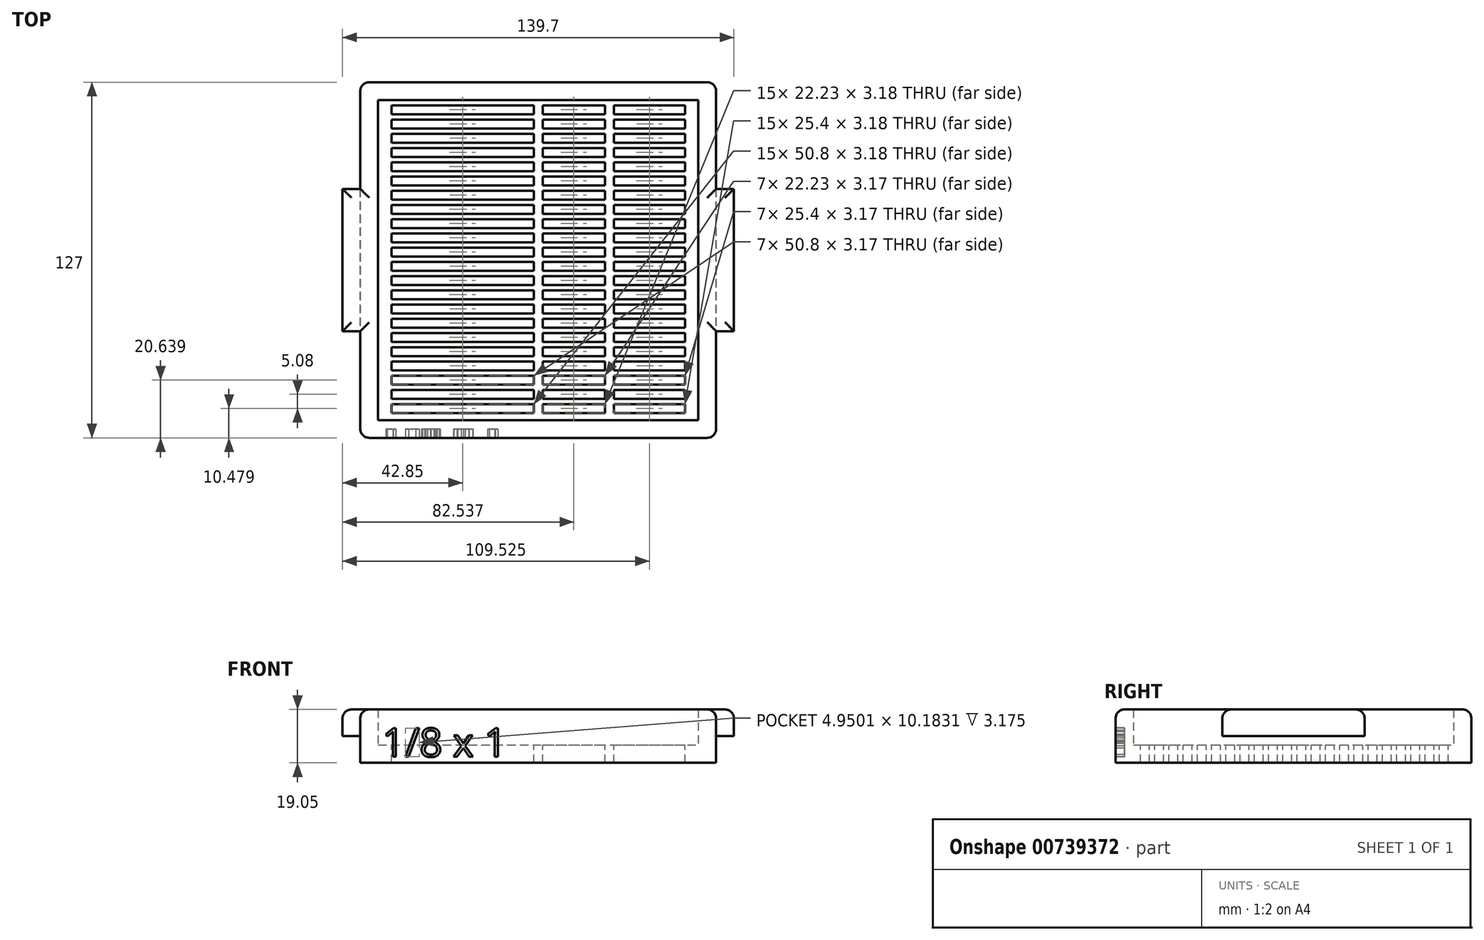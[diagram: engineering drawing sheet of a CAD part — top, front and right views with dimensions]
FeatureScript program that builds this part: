
annotation { "Feature Type Name" : "Feature", "Feature Type Description" : "" }
export const myFeature = defineFeature(function(context is Context, id is Id, definition is map)
    precondition{}
    {
        {
            var Q0;
            Q0=qCreatedBy(makeId("Top.planeOp"),FACE);
            var sketch = newSketch(context, id + "F0", { "sketchPlane" : qUnion([Q0])});
            skLineSegment(sketch, "E0.bottom", {"start": v(-63.5, -63.76) * mm, "end": v(63.5, -63.76) * mm});
            skLineSegment(sketch, "E0.top", {"start": v(-63.5, 63.24) * mm, "end": v(63.5, 63.24) * mm});
            skLineSegment(sketch, "E0.left", {"start": v(-63.5, -63.76) * mm, "end": v(-63.5, 63.24) * mm});
            skLineSegment(sketch, "E0.right", {"start": v(63.5, -63.76) * mm, "end": v(63.5, 63.24) * mm});
            skLineSegment(sketch, "E1.bottom", {"start": v(-57.15, -57.4) * mm, "end": v(57.15, -57.4) * mm});
            skLineSegment(sketch, "E1.top", {"start": v(-57.15, 56.9) * mm, "end": v(57.15, 56.9) * mm});
            skLineSegment(sketch, "E1.left", {"start": v(-57.15, -57.4) * mm, "end": v(-57.15, 56.9) * mm});
            skLineSegment(sketch, "E1.right", {"start": v(57.15, -57.4) * mm, "end": v(57.15, 56.9) * mm});
            skPoint(sketch, "E2", {"position": v(-63.5, -0.26) * mm});
            skPoint(sketch, "E3", {"position": v(63.5, -0.26) * mm});
            skLineSegment(sketch, "E4.bottom", {"start": v(-69.85, 25.14) * mm, "end": v(-57.15, 25.14) * mm});
            skLineSegment(sketch, "E4.top", {"start": v(-69.85, -25.66) * mm, "end": v(-57.15, -25.66) * mm});
            skLineSegment(sketch, "E4.left", {"start": v(-69.85, 25.14) * mm, "end": v(-69.85, -25.66) * mm});
            skLineSegment(sketch, "E4.right", {"start": v(-57.15, 25.14) * mm, "end": v(-57.15, -25.66) * mm});
            skLineSegment(sketch, "E5.bottom", {"start": v(69.85, 25.14) * mm, "end": v(57.15, 25.14) * mm});
            skLineSegment(sketch, "E5.top", {"start": v(69.85, -25.66) * mm, "end": v(57.15, -25.66) * mm});
            skLineSegment(sketch, "E5.left", {"start": v(69.85, 25.14) * mm, "end": v(69.85, -25.66) * mm});
            skLineSegment(sketch, "E5.right", {"start": v(57.15, 25.14) * mm, "end": v(57.15, -25.66) * mm});
            skPoint(sketch, "E5.cornerSnap0", {"position": v(-63.5, 25.14) * mm});
            skSolve(sketch);
        }
        {
            var Q0;
            {var subQ3=sQuery(id+"F0.wireOp",EDGE,"E1.bottom");Q0=makeQuery(id+"F0.imprint","IMPRINT",FACE,{"disambiguationData":[TD([[makeQuery(id+"F0.imprint","IMPRINT",EDGE,{"derivedFrom":subQ3}),1.0]])]});}
            extrude(context, id + "F1", {"entities" : qUnion([Q0]), "depth" : 6.35 * mm, "offsetDistance" : 25.4 * mm});
        }
        {
            var Q0;
            Q0 = qSketchRegion(id + "F0", true);
            extrude(context, id + "F2", {"entities" : qUnion([Q0]), "operationType" : NewBodyOperationType.ADD, "depth" : 19.05 * mm, "offsetDistance" : 25.4 * mm});
        }
        {
            var Q0;
            Q0=makeQuery(id+"F1.opExtrude","CAP_FACE",FACE,{"disambiguationData":[OSD([sQuery(id+"F0.wireOp",EDGE,"E1.bottom"),sQuery(id+"F0.wireOp",EDGE,"E1.top"),sQuery(id+"F0.wireOp",EDGE,"E1.left"),sQuery(id+"F0.wireOp",EDGE,"E1.right"),sQuery(id+"F0.wireOp",EDGE,"E4.right"),sQuery(id+"F0.wireOp",EDGE,"E5.right")])],"isStart":false});
            var sketch = newSketch(context, id + "F3", { "sketchPlane" : qUnion([Q0])});
            skLineSegment(sketch, "E6.bottom", {"start": v(-52.4, -54.87) * mm, "end": v(-23.83, -54.87) * mm});
            skLineSegment(sketch, "E6.top", {"start": v(-52.4, -51.7) * mm, "end": v(-23.83, -51.7) * mm});
            skLineSegment(sketch, "E6.left", {"start": v(-52.4, -54.87) * mm, "end": v(-52.4, -51.7) * mm});
            skLineSegment(sketch, "E6.right", {"start": v(-23.83, -54.87) * mm, "end": v(-23.83, -51.7) * mm});
            skLineSegment(sketch, "E7.0.1.0", {"start": v(-52.4, -49.79) * mm, "end": v(-23.83, -49.79) * mm});
            skLineSegment(sketch, "E7.0.1.1", {"start": v(-52.4, -46.61) * mm, "end": v(-23.83, -46.61) * mm});
            skLineSegment(sketch, "E7.0.1.2", {"start": v(-52.4, -49.79) * mm, "end": v(-52.4, -46.61) * mm});
            skLineSegment(sketch, "E7.0.1.3", {"start": v(-23.83, -49.79) * mm, "end": v(-23.83, -46.61) * mm});
            skLineSegment(sketch, "E7.0.2.0", {"start": v(-52.4, -44.7) * mm, "end": v(-23.83, -44.7) * mm});
            skLineSegment(sketch, "E7.0.2.1", {"start": v(-52.4, -41.53) * mm, "end": v(-23.83, -41.53) * mm});
            skLineSegment(sketch, "E7.0.2.2", {"start": v(-52.4, -44.7) * mm, "end": v(-52.4, -41.53) * mm});
            skLineSegment(sketch, "E7.0.2.3", {"start": v(-23.83, -44.7) * mm, "end": v(-23.83, -41.53) * mm});
            skLineSegment(sketch, "E7.0.3.0", {"start": v(-52.4, -39.63) * mm, "end": v(-23.83, -39.63) * mm});
            skLineSegment(sketch, "E7.0.3.1", {"start": v(-52.4, -36.45) * mm, "end": v(-23.83, -36.45) * mm});
            skLineSegment(sketch, "E7.0.3.2", {"start": v(-52.4, -39.63) * mm, "end": v(-52.4, -36.45) * mm});
            skLineSegment(sketch, "E7.0.3.3", {"start": v(-23.83, -39.63) * mm, "end": v(-23.83, -36.45) * mm});
            skLineSegment(sketch, "E7.0.4.0", {"start": v(-52.4, -34.55) * mm, "end": v(-23.83, -34.55) * mm});
            skLineSegment(sketch, "E7.0.4.1", {"start": v(-52.4, -31.37) * mm, "end": v(-23.83, -31.37) * mm});
            skLineSegment(sketch, "E7.0.4.2", {"start": v(-52.4, -34.55) * mm, "end": v(-52.4, -31.37) * mm});
            skLineSegment(sketch, "E7.0.4.3", {"start": v(-23.83, -34.55) * mm, "end": v(-23.83, -31.37) * mm});
            skLineSegment(sketch, "E7.0.5.0", {"start": v(-52.4, -29.47) * mm, "end": v(-23.83, -29.47) * mm});
            skLineSegment(sketch, "E7.0.5.1", {"start": v(-52.4, -26.3) * mm, "end": v(-23.83, -26.3) * mm});
            skLineSegment(sketch, "E7.0.5.2", {"start": v(-52.4, -29.47) * mm, "end": v(-52.4, -26.3) * mm});
            skLineSegment(sketch, "E7.0.5.3", {"start": v(-23.83, -29.47) * mm, "end": v(-23.83, -26.3) * mm});
            skLineSegment(sketch, "E7.0.6.0", {"start": v(-52.4, -24.39) * mm, "end": v(-23.83, -24.39) * mm});
            skLineSegment(sketch, "E7.0.6.1", {"start": v(-52.4, -21.21) * mm, "end": v(-23.83, -21.21) * mm});
            skLineSegment(sketch, "E7.0.6.2", {"start": v(-52.4, -24.39) * mm, "end": v(-52.4, -21.21) * mm});
            skLineSegment(sketch, "E7.0.6.3", {"start": v(-23.83, -24.39) * mm, "end": v(-23.83, -21.21) * mm});
            skLineSegment(sketch, "E7.0.7.0", {"start": v(-52.4, -19.3) * mm, "end": v(-23.83, -19.3) * mm});
            skLineSegment(sketch, "E7.0.7.1", {"start": v(-52.4, -16.13) * mm, "end": v(-23.83, -16.13) * mm});
            skLineSegment(sketch, "E7.0.7.2", {"start": v(-52.4, -19.3) * mm, "end": v(-52.4, -16.13) * mm});
            skLineSegment(sketch, "E7.0.7.3", {"start": v(-23.83, -19.3) * mm, "end": v(-23.83, -16.13) * mm});
            skLineSegment(sketch, "E7.0.8.0", {"start": v(-52.4, -14.23) * mm, "end": v(-23.83, -14.23) * mm});
            skLineSegment(sketch, "E7.0.8.1", {"start": v(-52.4, -11.05) * mm, "end": v(-23.83, -11.05) * mm});
            skLineSegment(sketch, "E7.0.8.2", {"start": v(-52.4, -14.23) * mm, "end": v(-52.4, -11.05) * mm});
            skLineSegment(sketch, "E7.0.8.3", {"start": v(-23.83, -14.23) * mm, "end": v(-23.83, -11.05) * mm});
            skLineSegment(sketch, "E7.0.9.0", {"start": v(-52.4, -9.15) * mm, "end": v(-23.83, -9.15) * mm});
            skLineSegment(sketch, "E7.0.9.1", {"start": v(-52.4, -5.97) * mm, "end": v(-23.83, -5.97) * mm});
            skLineSegment(sketch, "E7.0.9.2", {"start": v(-52.4, -9.15) * mm, "end": v(-52.4, -5.97) * mm});
            skLineSegment(sketch, "E7.0.9.3", {"start": v(-23.83, -9.15) * mm, "end": v(-23.83, -5.97) * mm});
            skLineSegment(sketch, "E7.0.10.0", {"start": v(-52.4, -4.07) * mm, "end": v(-23.83, -4.07) * mm});
            skLineSegment(sketch, "E7.0.10.1", {"start": v(-52.4, -0.9) * mm, "end": v(-23.83, -0.9) * mm});
            skLineSegment(sketch, "E7.0.10.2", {"start": v(-52.4, -4.07) * mm, "end": v(-52.4, -0.9) * mm});
            skLineSegment(sketch, "E7.0.10.3", {"start": v(-23.83, -4.07) * mm, "end": v(-23.83, -0.9) * mm});
            skLineSegment(sketch, "E7.0.11.0", {"start": v(-52.4, 1.01) * mm, "end": v(-23.83, 1.01) * mm});
            skLineSegment(sketch, "E7.0.11.1", {"start": v(-52.4, 4.19) * mm, "end": v(-23.83, 4.19) * mm});
            skLineSegment(sketch, "E7.0.11.2", {"start": v(-52.4, 1.01) * mm, "end": v(-52.4, 4.19) * mm});
            skLineSegment(sketch, "E7.0.11.3", {"start": v(-23.83, 1.01) * mm, "end": v(-23.83, 4.19) * mm});
            skLineSegment(sketch, "E7.0.12.0", {"start": v(-52.4, 6.1) * mm, "end": v(-23.83, 6.1) * mm});
            skLineSegment(sketch, "E7.0.12.1", {"start": v(-52.4, 9.27) * mm, "end": v(-23.83, 9.27) * mm});
            skLineSegment(sketch, "E7.0.12.2", {"start": v(-52.4, 6.1) * mm, "end": v(-52.4, 9.27) * mm});
            skLineSegment(sketch, "E7.0.12.3", {"start": v(-23.83, 6.1) * mm, "end": v(-23.83, 9.27) * mm});
            skLineSegment(sketch, "E7.0.13.0", {"start": v(-52.4, 11.17) * mm, "end": v(-23.83, 11.17) * mm});
            skLineSegment(sketch, "E7.0.13.1", {"start": v(-52.4, 14.35) * mm, "end": v(-23.83, 14.35) * mm});
            skLineSegment(sketch, "E7.0.13.2", {"start": v(-52.4, 11.17) * mm, "end": v(-52.4, 14.35) * mm});
            skLineSegment(sketch, "E7.0.13.3", {"start": v(-23.83, 11.17) * mm, "end": v(-23.83, 14.35) * mm});
            skLineSegment(sketch, "E7.0.14.0", {"start": v(-52.4, 16.25) * mm, "end": v(-23.83, 16.25) * mm});
            skLineSegment(sketch, "E7.0.14.1", {"start": v(-52.4, 19.43) * mm, "end": v(-23.83, 19.43) * mm});
            skLineSegment(sketch, "E7.0.14.2", {"start": v(-52.4, 16.25) * mm, "end": v(-52.4, 19.43) * mm});
            skLineSegment(sketch, "E7.0.14.3", {"start": v(-23.83, 16.25) * mm, "end": v(-23.83, 19.43) * mm});
            skLineSegment(sketch, "E7.0.15.0", {"start": v(-52.4, 21.33) * mm, "end": v(-23.83, 21.33) * mm});
            skLineSegment(sketch, "E7.0.15.1", {"start": v(-52.4, 24.5) * mm, "end": v(-23.83, 24.5) * mm});
            skLineSegment(sketch, "E7.0.15.2", {"start": v(-52.4, 21.33) * mm, "end": v(-52.4, 24.5) * mm});
            skLineSegment(sketch, "E7.0.15.3", {"start": v(-23.83, 21.33) * mm, "end": v(-23.83, 24.5) * mm});
            skLineSegment(sketch, "E7.0.16.0", {"start": v(-52.4, 26.41) * mm, "end": v(-23.83, 26.41) * mm});
            skLineSegment(sketch, "E7.0.16.1", {"start": v(-52.4, 29.59) * mm, "end": v(-23.83, 29.59) * mm});
            skLineSegment(sketch, "E7.0.16.2", {"start": v(-52.4, 26.41) * mm, "end": v(-52.4, 29.59) * mm});
            skLineSegment(sketch, "E7.0.16.3", {"start": v(-23.83, 26.41) * mm, "end": v(-23.83, 29.59) * mm});
            skLineSegment(sketch, "E7.0.17.0", {"start": v(-52.4, 31.5) * mm, "end": v(-23.83, 31.5) * mm});
            skLineSegment(sketch, "E7.0.17.1", {"start": v(-52.4, 34.67) * mm, "end": v(-23.83, 34.67) * mm});
            skLineSegment(sketch, "E7.0.17.2", {"start": v(-52.4, 31.5) * mm, "end": v(-52.4, 34.67) * mm});
            skLineSegment(sketch, "E7.0.17.3", {"start": v(-23.83, 31.5) * mm, "end": v(-23.83, 34.67) * mm});
            skLineSegment(sketch, "E7.0.18.0", {"start": v(-52.4, 36.57) * mm, "end": v(-23.83, 36.57) * mm});
            skLineSegment(sketch, "E7.0.18.1", {"start": v(-52.4, 39.75) * mm, "end": v(-23.83, 39.75) * mm});
            skLineSegment(sketch, "E7.0.18.2", {"start": v(-52.4, 36.57) * mm, "end": v(-52.4, 39.75) * mm});
            skLineSegment(sketch, "E7.0.18.3", {"start": v(-23.83, 36.57) * mm, "end": v(-23.83, 39.75) * mm});
            skLineSegment(sketch, "E7.0.19.0", {"start": v(-52.4, 41.65) * mm, "end": v(-23.83, 41.65) * mm});
            skLineSegment(sketch, "E7.0.19.1", {"start": v(-52.4, 44.83) * mm, "end": v(-23.83, 44.83) * mm});
            skLineSegment(sketch, "E7.0.19.2", {"start": v(-52.4, 41.65) * mm, "end": v(-52.4, 44.83) * mm});
            skLineSegment(sketch, "E7.0.19.3", {"start": v(-23.83, 41.65) * mm, "end": v(-23.83, 44.83) * mm});
            skLineSegment(sketch, "E7.0.20.0", {"start": v(-52.4, 46.73) * mm, "end": v(-23.83, 46.73) * mm});
            skLineSegment(sketch, "E7.0.20.1", {"start": v(-52.4, 49.9) * mm, "end": v(-23.83, 49.9) * mm});
            skLineSegment(sketch, "E7.0.20.2", {"start": v(-52.4, 46.73) * mm, "end": v(-52.4, 49.9) * mm});
            skLineSegment(sketch, "E7.0.20.3", {"start": v(-23.83, 46.73) * mm, "end": v(-23.83, 49.9) * mm});
            skLineSegment(sketch, "E7.0.21.0", {"start": v(-52.4, 51.81) * mm, "end": v(-23.83, 51.81) * mm});
            skLineSegment(sketch, "E7.0.21.1", {"start": v(-52.4, 54.99) * mm, "end": v(-23.83, 54.99) * mm});
            skLineSegment(sketch, "E7.0.21.2", {"start": v(-52.4, 51.81) * mm, "end": v(-52.4, 54.99) * mm});
            skLineSegment(sketch, "E7.0.21.3", {"start": v(-23.83, 51.81) * mm, "end": v(-23.83, 54.99) * mm});
            skLineSegment(sketch, "E7.1.0.0", {"start": v(-27, -54.87) * mm, "end": v(1.57, -54.87) * mm});
            skLineSegment(sketch, "E7.1.0.1", {"start": v(-27, -51.7) * mm, "end": v(1.57, -51.7) * mm});
            skLineSegment(sketch, "E7.1.0.2", {"start": v(-27, -54.87) * mm, "end": v(-27, -51.7) * mm});
            skLineSegment(sketch, "E7.1.0.3", {"start": v(1.57, -54.87) * mm, "end": v(1.57, -51.7) * mm});
            skLineSegment(sketch, "E7.1.1.0", {"start": v(-27, -49.79) * mm, "end": v(1.57, -49.79) * mm});
            skLineSegment(sketch, "E7.1.1.1", {"start": v(-27, -46.61) * mm, "end": v(1.57, -46.61) * mm});
            skLineSegment(sketch, "E7.1.1.2", {"start": v(-27, -49.79) * mm, "end": v(-27, -46.61) * mm});
            skLineSegment(sketch, "E7.1.1.3", {"start": v(1.57, -49.79) * mm, "end": v(1.57, -46.61) * mm});
            skLineSegment(sketch, "E7.1.2.0", {"start": v(-27, -44.7) * mm, "end": v(1.57, -44.7) * mm});
            skLineSegment(sketch, "E7.1.2.1", {"start": v(-27, -41.53) * mm, "end": v(1.57, -41.53) * mm});
            skLineSegment(sketch, "E7.1.2.2", {"start": v(-27, -44.7) * mm, "end": v(-27, -41.53) * mm});
            skLineSegment(sketch, "E7.1.2.3", {"start": v(1.57, -44.7) * mm, "end": v(1.57, -41.53) * mm});
            skLineSegment(sketch, "E7.1.3.0", {"start": v(-27, -39.63) * mm, "end": v(1.57, -39.63) * mm});
            skLineSegment(sketch, "E7.1.3.1", {"start": v(-27, -36.45) * mm, "end": v(1.57, -36.45) * mm});
            skLineSegment(sketch, "E7.1.3.2", {"start": v(-27, -39.63) * mm, "end": v(-27, -36.45) * mm});
            skLineSegment(sketch, "E7.1.3.3", {"start": v(1.57, -39.63) * mm, "end": v(1.57, -36.45) * mm});
            skLineSegment(sketch, "E7.1.4.0", {"start": v(-27, -34.55) * mm, "end": v(1.57, -34.55) * mm});
            skLineSegment(sketch, "E7.1.4.1", {"start": v(-27, -31.37) * mm, "end": v(1.57, -31.37) * mm});
            skLineSegment(sketch, "E7.1.4.2", {"start": v(-27, -34.55) * mm, "end": v(-27, -31.37) * mm});
            skLineSegment(sketch, "E7.1.4.3", {"start": v(1.57, -34.55) * mm, "end": v(1.57, -31.37) * mm});
            skLineSegment(sketch, "E7.1.5.0", {"start": v(-27, -29.47) * mm, "end": v(1.57, -29.47) * mm});
            skLineSegment(sketch, "E7.1.5.1", {"start": v(-27, -26.3) * mm, "end": v(1.57, -26.3) * mm});
            skLineSegment(sketch, "E7.1.5.2", {"start": v(-27, -29.47) * mm, "end": v(-27, -26.3) * mm});
            skLineSegment(sketch, "E7.1.5.3", {"start": v(1.57, -29.47) * mm, "end": v(1.57, -26.3) * mm});
            skLineSegment(sketch, "E7.1.6.0", {"start": v(-27, -24.39) * mm, "end": v(1.57, -24.39) * mm});
            skLineSegment(sketch, "E7.1.6.1", {"start": v(-27, -21.21) * mm, "end": v(1.57, -21.21) * mm});
            skLineSegment(sketch, "E7.1.6.2", {"start": v(-27, -24.39) * mm, "end": v(-27, -21.21) * mm});
            skLineSegment(sketch, "E7.1.6.3", {"start": v(1.57, -24.39) * mm, "end": v(1.57, -21.21) * mm});
            skLineSegment(sketch, "E7.1.7.0", {"start": v(-27, -19.3) * mm, "end": v(1.57, -19.3) * mm});
            skLineSegment(sketch, "E7.1.7.1", {"start": v(-27, -16.13) * mm, "end": v(1.57, -16.13) * mm});
            skLineSegment(sketch, "E7.1.7.2", {"start": v(-27, -19.3) * mm, "end": v(-27, -16.13) * mm});
            skLineSegment(sketch, "E7.1.7.3", {"start": v(1.57, -19.3) * mm, "end": v(1.57, -16.13) * mm});
            skLineSegment(sketch, "E7.1.8.0", {"start": v(-27, -14.23) * mm, "end": v(1.57, -14.23) * mm});
            skLineSegment(sketch, "E7.1.8.1", {"start": v(-27, -11.05) * mm, "end": v(1.57, -11.05) * mm});
            skLineSegment(sketch, "E7.1.8.2", {"start": v(-27, -14.23) * mm, "end": v(-27, -11.05) * mm});
            skLineSegment(sketch, "E7.1.8.3", {"start": v(1.57, -14.23) * mm, "end": v(1.57, -11.05) * mm});
            skLineSegment(sketch, "E7.1.9.0", {"start": v(-27, -9.15) * mm, "end": v(1.57, -9.15) * mm});
            skLineSegment(sketch, "E7.1.9.1", {"start": v(-27, -5.97) * mm, "end": v(1.57, -5.97) * mm});
            skLineSegment(sketch, "E7.1.9.2", {"start": v(-27, -9.15) * mm, "end": v(-27, -5.97) * mm});
            skLineSegment(sketch, "E7.1.9.3", {"start": v(1.57, -9.15) * mm, "end": v(1.57, -5.97) * mm});
            skLineSegment(sketch, "E7.1.10.0", {"start": v(-27, -4.07) * mm, "end": v(1.57, -4.07) * mm});
            skLineSegment(sketch, "E7.1.10.1", {"start": v(-27, -0.9) * mm, "end": v(1.57, -0.9) * mm});
            skLineSegment(sketch, "E7.1.10.2", {"start": v(-27, -4.07) * mm, "end": v(-27, -0.9) * mm});
            skLineSegment(sketch, "E7.1.10.3", {"start": v(1.57, -4.07) * mm, "end": v(1.57, -0.9) * mm});
            skLineSegment(sketch, "E7.1.11.0", {"start": v(-27, 1.01) * mm, "end": v(1.57, 1.01) * mm});
            skLineSegment(sketch, "E7.1.11.1", {"start": v(-27, 4.19) * mm, "end": v(1.57, 4.19) * mm});
            skLineSegment(sketch, "E7.1.11.2", {"start": v(-27, 1.01) * mm, "end": v(-27, 4.19) * mm});
            skLineSegment(sketch, "E7.1.11.3", {"start": v(1.57, 1.01) * mm, "end": v(1.57, 4.19) * mm});
            skLineSegment(sketch, "E7.1.12.0", {"start": v(-27, 6.1) * mm, "end": v(1.57, 6.1) * mm});
            skLineSegment(sketch, "E7.1.12.1", {"start": v(-27, 9.27) * mm, "end": v(1.57, 9.27) * mm});
            skLineSegment(sketch, "E7.1.12.2", {"start": v(-27, 6.1) * mm, "end": v(-27, 9.27) * mm});
            skLineSegment(sketch, "E7.1.12.3", {"start": v(1.57, 6.1) * mm, "end": v(1.57, 9.27) * mm});
            skLineSegment(sketch, "E7.1.13.0", {"start": v(-27, 11.17) * mm, "end": v(1.57, 11.17) * mm});
            skLineSegment(sketch, "E7.1.13.1", {"start": v(-27, 14.35) * mm, "end": v(1.57, 14.35) * mm});
            skLineSegment(sketch, "E7.1.13.2", {"start": v(-27, 11.17) * mm, "end": v(-27, 14.35) * mm});
            skLineSegment(sketch, "E7.1.13.3", {"start": v(1.57, 11.17) * mm, "end": v(1.57, 14.35) * mm});
            skLineSegment(sketch, "E7.1.14.0", {"start": v(-27, 16.25) * mm, "end": v(1.57, 16.25) * mm});
            skLineSegment(sketch, "E7.1.14.1", {"start": v(-27, 19.43) * mm, "end": v(1.57, 19.43) * mm});
            skLineSegment(sketch, "E7.1.14.2", {"start": v(-27, 16.25) * mm, "end": v(-27, 19.43) * mm});
            skLineSegment(sketch, "E7.1.14.3", {"start": v(1.57, 16.25) * mm, "end": v(1.57, 19.43) * mm});
            skLineSegment(sketch, "E7.1.15.0", {"start": v(-27, 21.33) * mm, "end": v(1.57, 21.33) * mm});
            skLineSegment(sketch, "E7.1.15.1", {"start": v(-27, 24.5) * mm, "end": v(1.57, 24.5) * mm});
            skLineSegment(sketch, "E7.1.15.2", {"start": v(-27, 21.33) * mm, "end": v(-27, 24.5) * mm});
            skLineSegment(sketch, "E7.1.15.3", {"start": v(1.57, 21.33) * mm, "end": v(1.57, 24.5) * mm});
            skLineSegment(sketch, "E7.1.16.0", {"start": v(-27, 26.41) * mm, "end": v(1.57, 26.41) * mm});
            skLineSegment(sketch, "E7.1.16.1", {"start": v(-27, 29.59) * mm, "end": v(1.57, 29.59) * mm});
            skLineSegment(sketch, "E7.1.16.2", {"start": v(-27, 26.41) * mm, "end": v(-27, 29.59) * mm});
            skLineSegment(sketch, "E7.1.16.3", {"start": v(1.57, 26.41) * mm, "end": v(1.57, 29.59) * mm});
            skLineSegment(sketch, "E7.1.17.0", {"start": v(-27, 31.5) * mm, "end": v(1.57, 31.5) * mm});
            skLineSegment(sketch, "E7.1.17.1", {"start": v(-27, 34.67) * mm, "end": v(1.57, 34.67) * mm});
            skLineSegment(sketch, "E7.1.17.2", {"start": v(-27, 31.5) * mm, "end": v(-27, 34.67) * mm});
            skLineSegment(sketch, "E7.1.17.3", {"start": v(1.57, 31.5) * mm, "end": v(1.57, 34.67) * mm});
            skLineSegment(sketch, "E7.1.18.0", {"start": v(-27, 36.57) * mm, "end": v(1.57, 36.57) * mm});
            skLineSegment(sketch, "E7.1.18.1", {"start": v(-27, 39.75) * mm, "end": v(1.57, 39.75) * mm});
            skLineSegment(sketch, "E7.1.18.2", {"start": v(-27, 36.57) * mm, "end": v(-27, 39.75) * mm});
            skLineSegment(sketch, "E7.1.18.3", {"start": v(1.57, 36.57) * mm, "end": v(1.57, 39.75) * mm});
            skLineSegment(sketch, "E7.1.19.0", {"start": v(-27, 41.65) * mm, "end": v(1.57, 41.65) * mm});
            skLineSegment(sketch, "E7.1.19.1", {"start": v(-27, 44.83) * mm, "end": v(1.57, 44.83) * mm});
            skLineSegment(sketch, "E7.1.19.2", {"start": v(-27, 41.65) * mm, "end": v(-27, 44.83) * mm});
            skLineSegment(sketch, "E7.1.19.3", {"start": v(1.57, 41.65) * mm, "end": v(1.57, 44.83) * mm});
            skLineSegment(sketch, "E7.1.20.0", {"start": v(-27, 46.73) * mm, "end": v(1.57, 46.73) * mm});
            skLineSegment(sketch, "E7.1.20.1", {"start": v(-27, 49.9) * mm, "end": v(1.57, 49.9) * mm});
            skLineSegment(sketch, "E7.1.20.2", {"start": v(-27, 46.73) * mm, "end": v(-27, 49.9) * mm});
            skLineSegment(sketch, "E7.1.20.3", {"start": v(1.57, 46.73) * mm, "end": v(1.57, 49.9) * mm});
            skLineSegment(sketch, "E7.1.21.0", {"start": v(-27, 51.81) * mm, "end": v(1.57, 51.81) * mm});
            skLineSegment(sketch, "E7.1.21.1", {"start": v(-27, 54.99) * mm, "end": v(1.57, 54.99) * mm});
            skLineSegment(sketch, "E7.1.21.2", {"start": v(-27, 51.81) * mm, "end": v(-27, 54.99) * mm});
            skLineSegment(sketch, "E7.1.21.3", {"start": v(1.57, 51.81) * mm, "end": v(1.57, 54.99) * mm});
            skLineSegment(sketch, "E7.2.0.0", {"start": v(-1.6, -54.87) * mm, "end": v(26.97, -54.87) * mm});
            skLineSegment(sketch, "E7.2.0.1", {"start": v(-1.6, -51.7) * mm, "end": v(26.97, -51.7) * mm});
            skLineSegment(sketch, "E7.2.0.2", {"start": v(-1.6, -54.87) * mm, "end": v(-1.6, -51.7) * mm});
            skLineSegment(sketch, "E7.2.0.3", {"start": v(26.97, -54.87) * mm, "end": v(26.97, -51.7) * mm});
            skLineSegment(sketch, "E7.2.1.0", {"start": v(-1.6, -49.79) * mm, "end": v(26.97, -49.79) * mm});
            skLineSegment(sketch, "E7.2.1.1", {"start": v(-1.6, -46.61) * mm, "end": v(26.97, -46.61) * mm});
            skLineSegment(sketch, "E7.2.1.2", {"start": v(-1.6, -49.79) * mm, "end": v(-1.6, -46.61) * mm});
            skLineSegment(sketch, "E7.2.1.3", {"start": v(26.97, -49.79) * mm, "end": v(26.97, -46.61) * mm});
            skLineSegment(sketch, "E7.2.2.0", {"start": v(-1.6, -44.7) * mm, "end": v(26.97, -44.7) * mm});
            skLineSegment(sketch, "E7.2.2.1", {"start": v(-1.6, -41.53) * mm, "end": v(26.97, -41.53) * mm});
            skLineSegment(sketch, "E7.2.2.2", {"start": v(-1.6, -44.7) * mm, "end": v(-1.6, -41.53) * mm});
            skLineSegment(sketch, "E7.2.2.3", {"start": v(26.97, -44.7) * mm, "end": v(26.97, -41.53) * mm});
            skLineSegment(sketch, "E7.2.3.0", {"start": v(-1.6, -39.63) * mm, "end": v(26.97, -39.63) * mm});
            skLineSegment(sketch, "E7.2.3.1", {"start": v(-1.6, -36.45) * mm, "end": v(26.97, -36.45) * mm});
            skLineSegment(sketch, "E7.2.3.2", {"start": v(-1.6, -39.63) * mm, "end": v(-1.6, -36.45) * mm});
            skLineSegment(sketch, "E7.2.3.3", {"start": v(26.97, -39.63) * mm, "end": v(26.97, -36.45) * mm});
            skLineSegment(sketch, "E7.2.4.0", {"start": v(-1.6, -34.55) * mm, "end": v(26.97, -34.55) * mm});
            skLineSegment(sketch, "E7.2.4.1", {"start": v(-1.6, -31.37) * mm, "end": v(26.97, -31.37) * mm});
            skLineSegment(sketch, "E7.2.4.2", {"start": v(-1.6, -34.55) * mm, "end": v(-1.6, -31.37) * mm});
            skLineSegment(sketch, "E7.2.4.3", {"start": v(26.97, -34.55) * mm, "end": v(26.97, -31.37) * mm});
            skLineSegment(sketch, "E7.2.5.0", {"start": v(-1.6, -29.47) * mm, "end": v(26.97, -29.47) * mm});
            skLineSegment(sketch, "E7.2.5.1", {"start": v(-1.6, -26.3) * mm, "end": v(26.97, -26.3) * mm});
            skLineSegment(sketch, "E7.2.5.2", {"start": v(-1.6, -29.47) * mm, "end": v(-1.6, -26.3) * mm});
            skLineSegment(sketch, "E7.2.5.3", {"start": v(26.97, -29.47) * mm, "end": v(26.97, -26.3) * mm});
            skLineSegment(sketch, "E7.2.6.0", {"start": v(-1.6, -24.39) * mm, "end": v(26.97, -24.39) * mm});
            skLineSegment(sketch, "E7.2.6.1", {"start": v(-1.6, -21.21) * mm, "end": v(26.97, -21.21) * mm});
            skLineSegment(sketch, "E7.2.6.2", {"start": v(-1.6, -24.39) * mm, "end": v(-1.6, -21.21) * mm});
            skLineSegment(sketch, "E7.2.6.3", {"start": v(26.97, -24.39) * mm, "end": v(26.97, -21.21) * mm});
            skLineSegment(sketch, "E7.2.7.0", {"start": v(-1.6, -19.3) * mm, "end": v(26.97, -19.3) * mm});
            skLineSegment(sketch, "E7.2.7.1", {"start": v(-1.6, -16.13) * mm, "end": v(26.97, -16.13) * mm});
            skLineSegment(sketch, "E7.2.7.2", {"start": v(-1.6, -19.3) * mm, "end": v(-1.6, -16.13) * mm});
            skLineSegment(sketch, "E7.2.7.3", {"start": v(26.97, -19.3) * mm, "end": v(26.97, -16.13) * mm});
            skLineSegment(sketch, "E7.2.8.0", {"start": v(-1.6, -14.23) * mm, "end": v(26.97, -14.23) * mm});
            skLineSegment(sketch, "E7.2.8.1", {"start": v(-1.6, -11.05) * mm, "end": v(26.97, -11.05) * mm});
            skLineSegment(sketch, "E7.2.8.2", {"start": v(-1.6, -14.23) * mm, "end": v(-1.6, -11.05) * mm});
            skLineSegment(sketch, "E7.2.8.3", {"start": v(26.97, -14.23) * mm, "end": v(26.97, -11.05) * mm});
            skLineSegment(sketch, "E7.2.9.0", {"start": v(-1.6, -9.15) * mm, "end": v(26.97, -9.15) * mm});
            skLineSegment(sketch, "E7.2.9.1", {"start": v(-1.6, -5.97) * mm, "end": v(26.97, -5.97) * mm});
            skLineSegment(sketch, "E7.2.9.2", {"start": v(-1.6, -9.15) * mm, "end": v(-1.6, -5.97) * mm});
            skLineSegment(sketch, "E7.2.9.3", {"start": v(26.97, -9.15) * mm, "end": v(26.97, -5.97) * mm});
            skLineSegment(sketch, "E7.2.10.0", {"start": v(-1.6, -4.07) * mm, "end": v(26.97, -4.07) * mm});
            skLineSegment(sketch, "E7.2.10.1", {"start": v(-1.6, -0.9) * mm, "end": v(26.97, -0.9) * mm});
            skLineSegment(sketch, "E7.2.10.2", {"start": v(-1.6, -4.07) * mm, "end": v(-1.6, -0.9) * mm});
            skLineSegment(sketch, "E7.2.10.3", {"start": v(26.97, -4.07) * mm, "end": v(26.97, -0.9) * mm});
            skLineSegment(sketch, "E7.2.11.0", {"start": v(-1.6, 1.01) * mm, "end": v(26.97, 1.01) * mm});
            skLineSegment(sketch, "E7.2.11.1", {"start": v(-1.6, 4.19) * mm, "end": v(26.97, 4.19) * mm});
            skLineSegment(sketch, "E7.2.11.2", {"start": v(-1.6, 1.01) * mm, "end": v(-1.6, 4.19) * mm});
            skLineSegment(sketch, "E7.2.11.3", {"start": v(26.97, 1.01) * mm, "end": v(26.97, 4.19) * mm});
            skLineSegment(sketch, "E7.2.12.0", {"start": v(-1.6, 6.1) * mm, "end": v(26.97, 6.1) * mm});
            skLineSegment(sketch, "E7.2.12.1", {"start": v(-1.6, 9.27) * mm, "end": v(26.97, 9.27) * mm});
            skLineSegment(sketch, "E7.2.12.2", {"start": v(-1.6, 6.1) * mm, "end": v(-1.6, 9.27) * mm});
            skLineSegment(sketch, "E7.2.12.3", {"start": v(26.97, 6.1) * mm, "end": v(26.97, 9.27) * mm});
            skLineSegment(sketch, "E7.2.13.0", {"start": v(-1.6, 11.17) * mm, "end": v(26.97, 11.17) * mm});
            skLineSegment(sketch, "E7.2.13.1", {"start": v(-1.6, 14.35) * mm, "end": v(26.97, 14.35) * mm});
            skLineSegment(sketch, "E7.2.13.2", {"start": v(-1.6, 11.17) * mm, "end": v(-1.6, 14.35) * mm});
            skLineSegment(sketch, "E7.2.13.3", {"start": v(26.97, 11.17) * mm, "end": v(26.97, 14.35) * mm});
            skLineSegment(sketch, "E7.2.14.0", {"start": v(-1.6, 16.25) * mm, "end": v(26.97, 16.25) * mm});
            skLineSegment(sketch, "E7.2.14.1", {"start": v(-1.6, 19.43) * mm, "end": v(26.97, 19.43) * mm});
            skLineSegment(sketch, "E7.2.14.2", {"start": v(-1.6, 16.25) * mm, "end": v(-1.6, 19.43) * mm});
            skLineSegment(sketch, "E7.2.14.3", {"start": v(26.97, 16.25) * mm, "end": v(26.97, 19.43) * mm});
            skLineSegment(sketch, "E7.2.15.0", {"start": v(-1.6, 21.33) * mm, "end": v(26.97, 21.33) * mm});
            skLineSegment(sketch, "E7.2.15.1", {"start": v(-1.6, 24.5) * mm, "end": v(26.97, 24.5) * mm});
            skLineSegment(sketch, "E7.2.15.2", {"start": v(-1.6, 21.33) * mm, "end": v(-1.6, 24.5) * mm});
            skLineSegment(sketch, "E7.2.15.3", {"start": v(26.97, 21.33) * mm, "end": v(26.97, 24.5) * mm});
            skLineSegment(sketch, "E7.2.16.0", {"start": v(-1.6, 26.41) * mm, "end": v(26.97, 26.41) * mm});
            skLineSegment(sketch, "E7.2.16.1", {"start": v(-1.6, 29.59) * mm, "end": v(26.97, 29.59) * mm});
            skLineSegment(sketch, "E7.2.16.2", {"start": v(-1.6, 26.41) * mm, "end": v(-1.6, 29.59) * mm});
            skLineSegment(sketch, "E7.2.16.3", {"start": v(26.97, 26.41) * mm, "end": v(26.97, 29.59) * mm});
            skLineSegment(sketch, "E7.2.17.0", {"start": v(-1.6, 31.5) * mm, "end": v(26.97, 31.5) * mm});
            skLineSegment(sketch, "E7.2.17.1", {"start": v(-1.6, 34.67) * mm, "end": v(26.97, 34.67) * mm});
            skLineSegment(sketch, "E7.2.17.2", {"start": v(-1.6, 31.5) * mm, "end": v(-1.6, 34.67) * mm});
            skLineSegment(sketch, "E7.2.17.3", {"start": v(26.97, 31.5) * mm, "end": v(26.97, 34.67) * mm});
            skLineSegment(sketch, "E7.2.18.0", {"start": v(-1.6, 36.57) * mm, "end": v(26.97, 36.57) * mm});
            skLineSegment(sketch, "E7.2.18.1", {"start": v(-1.6, 39.75) * mm, "end": v(26.97, 39.75) * mm});
            skLineSegment(sketch, "E7.2.18.2", {"start": v(-1.6, 36.57) * mm, "end": v(-1.6, 39.75) * mm});
            skLineSegment(sketch, "E7.2.18.3", {"start": v(26.97, 36.57) * mm, "end": v(26.97, 39.75) * mm});
            skLineSegment(sketch, "E7.2.19.0", {"start": v(-1.6, 41.65) * mm, "end": v(26.97, 41.65) * mm});
            skLineSegment(sketch, "E7.2.19.1", {"start": v(-1.6, 44.83) * mm, "end": v(26.97, 44.83) * mm});
            skLineSegment(sketch, "E7.2.19.2", {"start": v(-1.6, 41.65) * mm, "end": v(-1.6, 44.83) * mm});
            skLineSegment(sketch, "E7.2.19.3", {"start": v(26.97, 41.65) * mm, "end": v(26.97, 44.83) * mm});
            skLineSegment(sketch, "E7.2.20.0", {"start": v(-1.6, 46.73) * mm, "end": v(26.97, 46.73) * mm});
            skLineSegment(sketch, "E7.2.20.1", {"start": v(-1.6, 49.9) * mm, "end": v(26.97, 49.9) * mm});
            skLineSegment(sketch, "E7.2.20.2", {"start": v(-1.6, 46.73) * mm, "end": v(-1.6, 49.9) * mm});
            skLineSegment(sketch, "E7.2.20.3", {"start": v(26.97, 46.73) * mm, "end": v(26.97, 49.9) * mm});
            skLineSegment(sketch, "E7.2.21.0", {"start": v(-1.6, 51.81) * mm, "end": v(26.97, 51.81) * mm});
            skLineSegment(sketch, "E7.2.21.1", {"start": v(-1.6, 54.99) * mm, "end": v(26.97, 54.99) * mm});
            skLineSegment(sketch, "E7.2.21.2", {"start": v(-1.6, 51.81) * mm, "end": v(-1.6, 54.99) * mm});
            skLineSegment(sketch, "E7.2.21.3", {"start": v(26.97, 51.81) * mm, "end": v(26.97, 54.99) * mm});
            skLineSegment(sketch, "E7.3.0.0", {"start": v(23.8, -54.87) * mm, "end": v(52.37, -54.87) * mm});
            skLineSegment(sketch, "E7.3.0.1", {"start": v(23.8, -51.7) * mm, "end": v(52.37, -51.7) * mm});
            skLineSegment(sketch, "E7.3.0.2", {"start": v(23.8, -54.87) * mm, "end": v(23.8, -51.7) * mm});
            skLineSegment(sketch, "E7.3.0.3", {"start": v(52.37, -54.87) * mm, "end": v(52.37, -51.7) * mm});
            skLineSegment(sketch, "E7.3.1.0", {"start": v(23.8, -49.79) * mm, "end": v(52.37, -49.79) * mm});
            skLineSegment(sketch, "E7.3.1.1", {"start": v(23.8, -46.61) * mm, "end": v(52.37, -46.61) * mm});
            skLineSegment(sketch, "E7.3.1.2", {"start": v(23.8, -49.79) * mm, "end": v(23.8, -46.61) * mm});
            skLineSegment(sketch, "E7.3.1.3", {"start": v(52.37, -49.79) * mm, "end": v(52.37, -46.61) * mm});
            skLineSegment(sketch, "E7.3.2.0", {"start": v(23.8, -44.7) * mm, "end": v(52.37, -44.7) * mm});
            skLineSegment(sketch, "E7.3.2.1", {"start": v(23.8, -41.53) * mm, "end": v(52.37, -41.53) * mm});
            skLineSegment(sketch, "E7.3.2.2", {"start": v(23.8, -44.7) * mm, "end": v(23.8, -41.53) * mm});
            skLineSegment(sketch, "E7.3.2.3", {"start": v(52.37, -44.7) * mm, "end": v(52.37, -41.53) * mm});
            skLineSegment(sketch, "E7.3.3.0", {"start": v(23.8, -39.63) * mm, "end": v(52.37, -39.63) * mm});
            skLineSegment(sketch, "E7.3.3.1", {"start": v(23.8, -36.45) * mm, "end": v(52.37, -36.45) * mm});
            skLineSegment(sketch, "E7.3.3.2", {"start": v(23.8, -39.63) * mm, "end": v(23.8, -36.45) * mm});
            skLineSegment(sketch, "E7.3.3.3", {"start": v(52.37, -39.63) * mm, "end": v(52.37, -36.45) * mm});
            skLineSegment(sketch, "E7.3.4.0", {"start": v(23.8, -34.55) * mm, "end": v(52.37, -34.55) * mm});
            skLineSegment(sketch, "E7.3.4.1", {"start": v(23.8, -31.37) * mm, "end": v(52.37, -31.37) * mm});
            skLineSegment(sketch, "E7.3.4.2", {"start": v(23.8, -34.55) * mm, "end": v(23.8, -31.37) * mm});
            skLineSegment(sketch, "E7.3.4.3", {"start": v(52.37, -34.55) * mm, "end": v(52.37, -31.37) * mm});
            skLineSegment(sketch, "E7.3.5.0", {"start": v(23.8, -29.47) * mm, "end": v(52.37, -29.47) * mm});
            skLineSegment(sketch, "E7.3.5.1", {"start": v(23.8, -26.3) * mm, "end": v(52.37, -26.3) * mm});
            skLineSegment(sketch, "E7.3.5.2", {"start": v(23.8, -29.47) * mm, "end": v(23.8, -26.3) * mm});
            skLineSegment(sketch, "E7.3.5.3", {"start": v(52.37, -29.47) * mm, "end": v(52.37, -26.3) * mm});
            skLineSegment(sketch, "E7.3.6.0", {"start": v(23.8, -24.39) * mm, "end": v(52.37, -24.39) * mm});
            skLineSegment(sketch, "E7.3.6.1", {"start": v(23.8, -21.21) * mm, "end": v(52.37, -21.21) * mm});
            skLineSegment(sketch, "E7.3.6.2", {"start": v(23.8, -24.39) * mm, "end": v(23.8, -21.21) * mm});
            skLineSegment(sketch, "E7.3.6.3", {"start": v(52.37, -24.39) * mm, "end": v(52.37, -21.21) * mm});
            skLineSegment(sketch, "E7.3.7.0", {"start": v(23.8, -19.3) * mm, "end": v(52.37, -19.3) * mm});
            skLineSegment(sketch, "E7.3.7.1", {"start": v(23.8, -16.13) * mm, "end": v(52.37, -16.13) * mm});
            skLineSegment(sketch, "E7.3.7.2", {"start": v(23.8, -19.3) * mm, "end": v(23.8, -16.13) * mm});
            skLineSegment(sketch, "E7.3.7.3", {"start": v(52.37, -19.3) * mm, "end": v(52.37, -16.13) * mm});
            skLineSegment(sketch, "E7.3.8.0", {"start": v(23.8, -14.23) * mm, "end": v(52.37, -14.23) * mm});
            skLineSegment(sketch, "E7.3.8.1", {"start": v(23.8, -11.05) * mm, "end": v(52.37, -11.05) * mm});
            skLineSegment(sketch, "E7.3.8.2", {"start": v(23.8, -14.23) * mm, "end": v(23.8, -11.05) * mm});
            skLineSegment(sketch, "E7.3.8.3", {"start": v(52.37, -14.23) * mm, "end": v(52.37, -11.05) * mm});
            skLineSegment(sketch, "E7.3.9.0", {"start": v(23.8, -9.15) * mm, "end": v(52.37, -9.15) * mm});
            skLineSegment(sketch, "E7.3.9.1", {"start": v(23.8, -5.97) * mm, "end": v(52.37, -5.97) * mm});
            skLineSegment(sketch, "E7.3.9.2", {"start": v(23.8, -9.15) * mm, "end": v(23.8, -5.97) * mm});
            skLineSegment(sketch, "E7.3.9.3", {"start": v(52.37, -9.15) * mm, "end": v(52.37, -5.97) * mm});
            skLineSegment(sketch, "E7.3.10.0", {"start": v(23.8, -4.07) * mm, "end": v(52.37, -4.07) * mm});
            skLineSegment(sketch, "E7.3.10.1", {"start": v(23.8, -0.9) * mm, "end": v(52.37, -0.9) * mm});
            skLineSegment(sketch, "E7.3.10.2", {"start": v(23.8, -4.07) * mm, "end": v(23.8, -0.9) * mm});
            skLineSegment(sketch, "E7.3.10.3", {"start": v(52.37, -4.07) * mm, "end": v(52.37, -0.9) * mm});
            skLineSegment(sketch, "E7.3.11.0", {"start": v(23.8, 1.01) * mm, "end": v(52.37, 1.01) * mm});
            skLineSegment(sketch, "E7.3.11.1", {"start": v(23.8, 4.19) * mm, "end": v(52.37, 4.19) * mm});
            skLineSegment(sketch, "E7.3.11.2", {"start": v(23.8, 1.01) * mm, "end": v(23.8, 4.19) * mm});
            skLineSegment(sketch, "E7.3.11.3", {"start": v(52.37, 1.01) * mm, "end": v(52.37, 4.19) * mm});
            skLineSegment(sketch, "E7.3.12.0", {"start": v(23.8, 6.1) * mm, "end": v(52.37, 6.1) * mm});
            skLineSegment(sketch, "E7.3.12.1", {"start": v(23.8, 9.27) * mm, "end": v(52.37, 9.27) * mm});
            skLineSegment(sketch, "E7.3.12.2", {"start": v(23.8, 6.1) * mm, "end": v(23.8, 9.27) * mm});
            skLineSegment(sketch, "E7.3.12.3", {"start": v(52.37, 6.1) * mm, "end": v(52.37, 9.27) * mm});
            skLineSegment(sketch, "E7.3.13.0", {"start": v(23.8, 11.17) * mm, "end": v(52.37, 11.17) * mm});
            skLineSegment(sketch, "E7.3.13.1", {"start": v(23.8, 14.35) * mm, "end": v(52.37, 14.35) * mm});
            skLineSegment(sketch, "E7.3.13.2", {"start": v(23.8, 11.17) * mm, "end": v(23.8, 14.35) * mm});
            skLineSegment(sketch, "E7.3.13.3", {"start": v(52.37, 11.17) * mm, "end": v(52.37, 14.35) * mm});
            skLineSegment(sketch, "E7.3.14.0", {"start": v(23.8, 16.25) * mm, "end": v(52.37, 16.25) * mm});
            skLineSegment(sketch, "E7.3.14.1", {"start": v(23.8, 19.43) * mm, "end": v(52.37, 19.43) * mm});
            skLineSegment(sketch, "E7.3.14.2", {"start": v(23.8, 16.25) * mm, "end": v(23.8, 19.43) * mm});
            skLineSegment(sketch, "E7.3.14.3", {"start": v(52.37, 16.25) * mm, "end": v(52.37, 19.43) * mm});
            skLineSegment(sketch, "E7.3.15.0", {"start": v(23.8, 21.33) * mm, "end": v(52.37, 21.33) * mm});
            skLineSegment(sketch, "E7.3.15.1", {"start": v(23.8, 24.5) * mm, "end": v(52.37, 24.5) * mm});
            skLineSegment(sketch, "E7.3.15.2", {"start": v(23.8, 21.33) * mm, "end": v(23.8, 24.5) * mm});
            skLineSegment(sketch, "E7.3.15.3", {"start": v(52.37, 21.33) * mm, "end": v(52.37, 24.5) * mm});
            skLineSegment(sketch, "E7.3.16.0", {"start": v(23.8, 26.41) * mm, "end": v(52.37, 26.41) * mm});
            skLineSegment(sketch, "E7.3.16.1", {"start": v(23.8, 29.59) * mm, "end": v(52.37, 29.59) * mm});
            skLineSegment(sketch, "E7.3.16.2", {"start": v(23.8, 26.41) * mm, "end": v(23.8, 29.59) * mm});
            skLineSegment(sketch, "E7.3.16.3", {"start": v(52.37, 26.41) * mm, "end": v(52.37, 29.59) * mm});
            skLineSegment(sketch, "E7.3.17.0", {"start": v(23.8, 31.5) * mm, "end": v(52.37, 31.5) * mm});
            skLineSegment(sketch, "E7.3.17.1", {"start": v(23.8, 34.67) * mm, "end": v(52.37, 34.67) * mm});
            skLineSegment(sketch, "E7.3.17.2", {"start": v(23.8, 31.5) * mm, "end": v(23.8, 34.67) * mm});
            skLineSegment(sketch, "E7.3.17.3", {"start": v(52.37, 31.5) * mm, "end": v(52.37, 34.67) * mm});
            skLineSegment(sketch, "E7.3.18.0", {"start": v(23.8, 36.57) * mm, "end": v(52.37, 36.57) * mm});
            skLineSegment(sketch, "E7.3.18.1", {"start": v(23.8, 39.75) * mm, "end": v(52.37, 39.75) * mm});
            skLineSegment(sketch, "E7.3.18.2", {"start": v(23.8, 36.57) * mm, "end": v(23.8, 39.75) * mm});
            skLineSegment(sketch, "E7.3.18.3", {"start": v(52.37, 36.57) * mm, "end": v(52.37, 39.75) * mm});
            skLineSegment(sketch, "E7.3.19.0", {"start": v(23.8, 41.65) * mm, "end": v(52.37, 41.65) * mm});
            skLineSegment(sketch, "E7.3.19.1", {"start": v(23.8, 44.83) * mm, "end": v(52.37, 44.83) * mm});
            skLineSegment(sketch, "E7.3.19.2", {"start": v(23.8, 41.65) * mm, "end": v(23.8, 44.83) * mm});
            skLineSegment(sketch, "E7.3.19.3", {"start": v(52.37, 41.65) * mm, "end": v(52.37, 44.83) * mm});
            skLineSegment(sketch, "E7.3.20.0", {"start": v(23.8, 46.73) * mm, "end": v(52.37, 46.73) * mm});
            skLineSegment(sketch, "E7.3.20.1", {"start": v(23.8, 49.9) * mm, "end": v(52.37, 49.9) * mm});
            skLineSegment(sketch, "E7.3.20.2", {"start": v(23.8, 46.73) * mm, "end": v(23.8, 49.9) * mm});
            skLineSegment(sketch, "E7.3.20.3", {"start": v(52.37, 46.73) * mm, "end": v(52.37, 49.9) * mm});
            skLineSegment(sketch, "E7.3.21.0", {"start": v(23.8, 51.81) * mm, "end": v(52.37, 51.81) * mm});
            skLineSegment(sketch, "E7.3.21.1", {"start": v(23.8, 54.99) * mm, "end": v(52.37, 54.99) * mm});
            skLineSegment(sketch, "E7.3.21.2", {"start": v(23.8, 51.81) * mm, "end": v(23.8, 54.99) * mm});
            skLineSegment(sketch, "E7.3.21.3", {"start": v(52.37, 51.81) * mm, "end": v(52.37, 54.99) * mm});
            skLineSegment(sketch, "E7.direction1", {"start": v(-52.4, -54.87) * mm, "end": v(-27, -54.87) * mm, "construction": true});
            skLineSegment(sketch, "E7.direction2", {"start": v(-52.4, -54.87) * mm, "end": v(-52.4, -49.79) * mm, "construction": true});
            skSolve(sketch);
        }
        {
            var Q0;
            Q0=makeQuery(id+"F3.imprint","IMPRINT",FACE,{"disambiguationData":[TD([[makeQuery(id+"F3.imprint","IMPRINT",EDGE,{"derivedFrom":sQuery(id+"F3.wireOp",EDGE,"E6.bottom")}),1.0]])]});
            var Q1;
            Q1=makeQuery(id+"F3.imprint","IMPRINT",FACE,{"disambiguationData":[TD([[makeQuery(id+"F3.imprint","IMPRINT",EDGE,{"derivedFrom":sQuery(id+"F3.wireOp",EDGE,"E7.0.1.0")}),1.0]])]});
            var Q2;
            Q2=makeQuery(id+"F3.imprint","IMPRINT",FACE,{"disambiguationData":[TD([[makeQuery(id+"F3.imprint","IMPRINT",EDGE,{"derivedFrom":sQuery(id+"F3.wireOp",EDGE,"E7.0.2.0")}),1.0]])]});
            var Q3;
            Q3=makeQuery(id+"F3.imprint","IMPRINT",FACE,{"disambiguationData":[TD([[makeQuery(id+"F3.imprint","IMPRINT",EDGE,{"derivedFrom":sQuery(id+"F3.wireOp",EDGE,"E7.0.3.0")}),1.0]])]});
            var Q4;
            Q4=makeQuery(id+"F3.imprint","IMPRINT",FACE,{"disambiguationData":[TD([[makeQuery(id+"F3.imprint","IMPRINT",EDGE,{"derivedFrom":sQuery(id+"F3.wireOp",EDGE,"E7.0.4.0")}),1.0]])]});
            var Q5;
            Q5=makeQuery(id+"F3.imprint","IMPRINT",FACE,{"disambiguationData":[TD([[makeQuery(id+"F3.imprint","IMPRINT",EDGE,{"derivedFrom":sQuery(id+"F3.wireOp",EDGE,"E7.0.5.0")}),1.0]])]});
            var Q6;
            Q6=makeQuery(id+"F3.imprint","IMPRINT",FACE,{"disambiguationData":[TD([[makeQuery(id+"F3.imprint","IMPRINT",EDGE,{"derivedFrom":sQuery(id+"F3.wireOp",EDGE,"E7.0.6.0")}),1.0]])]});
            var Q7;
            Q7=makeQuery(id+"F3.imprint","IMPRINT",FACE,{"disambiguationData":[TD([[makeQuery(id+"F3.imprint","IMPRINT",EDGE,{"derivedFrom":sQuery(id+"F3.wireOp",EDGE,"E7.0.7.0")}),1.0]])]});
            var Q8;
            Q8=makeQuery(id+"F3.imprint","IMPRINT",FACE,{"disambiguationData":[TD([[makeQuery(id+"F3.imprint","IMPRINT",EDGE,{"derivedFrom":sQuery(id+"F3.wireOp",EDGE,"E7.0.8.0")}),1.0]])]});
            var Q9;
            Q9=makeQuery(id+"F3.imprint","IMPRINT",FACE,{"disambiguationData":[TD([[makeQuery(id+"F3.imprint","IMPRINT",EDGE,{"derivedFrom":sQuery(id+"F3.wireOp",EDGE,"E7.0.9.0")}),1.0]])]});
            var Q10;
            Q10=makeQuery(id+"F3.imprint","IMPRINT",FACE,{"disambiguationData":[TD([[makeQuery(id+"F3.imprint","IMPRINT",EDGE,{"derivedFrom":sQuery(id+"F3.wireOp",EDGE,"E7.0.10.0")}),1.0]])]});
            var Q11;
            Q11=makeQuery(id+"F3.imprint","IMPRINT",FACE,{"disambiguationData":[TD([[makeQuery(id+"F3.imprint","IMPRINT",EDGE,{"derivedFrom":sQuery(id+"F3.wireOp",EDGE,"E7.0.11.0")}),1.0]])]});
            var Q12;
            Q12=makeQuery(id+"F3.imprint","IMPRINT",FACE,{"disambiguationData":[TD([[makeQuery(id+"F3.imprint","IMPRINT",EDGE,{"derivedFrom":sQuery(id+"F3.wireOp",EDGE,"E7.0.12.0")}),1.0]])]});
            var Q13;
            Q13=makeQuery(id+"F3.imprint","IMPRINT",FACE,{"disambiguationData":[TD([[makeQuery(id+"F3.imprint","IMPRINT",EDGE,{"derivedFrom":sQuery(id+"F3.wireOp",EDGE,"E7.0.13.0")}),1.0]])]});
            var Q14;
            Q14=makeQuery(id+"F3.imprint","IMPRINT",FACE,{"disambiguationData":[TD([[makeQuery(id+"F3.imprint","IMPRINT",EDGE,{"derivedFrom":sQuery(id+"F3.wireOp",EDGE,"E7.0.14.0")}),1.0]])]});
            var Q15;
            Q15=makeQuery(id+"F3.imprint","IMPRINT",FACE,{"disambiguationData":[TD([[makeQuery(id+"F3.imprint","IMPRINT",EDGE,{"derivedFrom":sQuery(id+"F3.wireOp",EDGE,"E7.0.15.0")}),1.0]])]});
            var Q16;
            Q16=makeQuery(id+"F3.imprint","IMPRINT",FACE,{"disambiguationData":[TD([[makeQuery(id+"F3.imprint","IMPRINT",EDGE,{"derivedFrom":sQuery(id+"F3.wireOp",EDGE,"E7.0.16.0")}),1.0]])]});
            var Q17;
            Q17=makeQuery(id+"F3.imprint","IMPRINT",FACE,{"disambiguationData":[TD([[makeQuery(id+"F3.imprint","IMPRINT",EDGE,{"derivedFrom":sQuery(id+"F3.wireOp",EDGE,"E7.0.17.0")}),1.0]])]});
            var Q18;
            Q18=makeQuery(id+"F3.imprint","IMPRINT",FACE,{"disambiguationData":[TD([[makeQuery(id+"F3.imprint","IMPRINT",EDGE,{"derivedFrom":sQuery(id+"F3.wireOp",EDGE,"E7.0.18.0")}),1.0]])]});
            var Q19;
            Q19=makeQuery(id+"F3.imprint","IMPRINT",FACE,{"disambiguationData":[TD([[makeQuery(id+"F3.imprint","IMPRINT",EDGE,{"derivedFrom":sQuery(id+"F3.wireOp",EDGE,"E7.0.19.0")}),1.0]])]});
            var Q20;
            Q20=makeQuery(id+"F3.imprint","IMPRINT",FACE,{"disambiguationData":[TD([[makeQuery(id+"F3.imprint","IMPRINT",EDGE,{"derivedFrom":sQuery(id+"F3.wireOp",EDGE,"E7.0.20.0")}),1.0]])]});
            var Q21;
            Q21=makeQuery(id+"F3.imprint","IMPRINT",FACE,{"disambiguationData":[TD([[makeQuery(id+"F3.imprint","IMPRINT",EDGE,{"derivedFrom":sQuery(id+"F3.wireOp",EDGE,"E7.0.21.0")}),1.0]])]});
            var Q22;
            {var subQ0=sQuery(id+"F3.wireOp",EDGE,"E6.right");Q22=makeQuery(id+"F3.imprint","IMPRINT",FACE,{"disambiguationData":[TD([[makeQuery(id+"F3.imprint","IMPRINT",EDGE,{"derivedFrom":subQ0}),-1.0]])]});}
            var Q23;
            {var subQ0=sQuery(id+"F3.wireOp",EDGE,"E7.0.1.3");Q23=makeQuery(id+"F3.imprint","IMPRINT",FACE,{"disambiguationData":[TD([[makeQuery(id+"F3.imprint","IMPRINT",EDGE,{"derivedFrom":subQ0}),-1.0]])]});}
            var Q24;
            {var subQ0=sQuery(id+"F3.wireOp",EDGE,"E7.1.0.3");Q24=makeQuery(id+"F3.imprint","IMPRINT",FACE,{"disambiguationData":[TD([[makeQuery(id+"F3.imprint","IMPRINT",EDGE,{"derivedFrom":subQ0}),-1.0]])]});}
            var Q25;
            {var subQ0=sQuery(id+"F3.wireOp",EDGE,"E7.1.1.3");Q25=makeQuery(id+"F3.imprint","IMPRINT",FACE,{"disambiguationData":[TD([[makeQuery(id+"F3.imprint","IMPRINT",EDGE,{"derivedFrom":subQ0}),-1.0]])]});}
            var Q26;
            {var subQ0=sQuery(id+"F3.wireOp",EDGE,"E7.2.0.3");Q26=makeQuery(id+"F3.imprint","IMPRINT",FACE,{"disambiguationData":[TD([[makeQuery(id+"F3.imprint","IMPRINT",EDGE,{"derivedFrom":subQ0}),-1.0]])]});}
            var Q27;
            {var subQ0=sQuery(id+"F3.wireOp",EDGE,"E7.2.1.3");Q27=makeQuery(id+"F3.imprint","IMPRINT",FACE,{"disambiguationData":[TD([[makeQuery(id+"F3.imprint","IMPRINT",EDGE,{"derivedFrom":subQ0}),-1.0]])]});}
            var Q28;
            {var subQ0=sQuery(id+"F3.wireOp",EDGE,"E7.2.2.3");Q28=makeQuery(id+"F3.imprint","IMPRINT",FACE,{"disambiguationData":[TD([[makeQuery(id+"F3.imprint","IMPRINT",EDGE,{"derivedFrom":subQ0}),-1.0]])]});}
            var Q29;
            {var subQ0=sQuery(id+"F3.wireOp",EDGE,"E7.2.3.3");Q29=makeQuery(id+"F3.imprint","IMPRINT",FACE,{"disambiguationData":[TD([[makeQuery(id+"F3.imprint","IMPRINT",EDGE,{"derivedFrom":subQ0}),-1.0]])]});}
            var Q30;
            {var subQ0=sQuery(id+"F3.wireOp",EDGE,"E7.1.3.3");Q30=makeQuery(id+"F3.imprint","IMPRINT",FACE,{"disambiguationData":[TD([[makeQuery(id+"F3.imprint","IMPRINT",EDGE,{"derivedFrom":subQ0}),-1.0]])]});}
            var Q31;
            {var subQ0=sQuery(id+"F3.wireOp",EDGE,"E7.1.2.3");Q31=makeQuery(id+"F3.imprint","IMPRINT",FACE,{"disambiguationData":[TD([[makeQuery(id+"F3.imprint","IMPRINT",EDGE,{"derivedFrom":subQ0}),-1.0]])]});}
            var Q32;
            {var subQ0=sQuery(id+"F3.wireOp",EDGE,"E7.0.2.3");Q32=makeQuery(id+"F3.imprint","IMPRINT",FACE,{"disambiguationData":[TD([[makeQuery(id+"F3.imprint","IMPRINT",EDGE,{"derivedFrom":subQ0}),-1.0]])]});}
            var Q33;
            {var subQ0=sQuery(id+"F3.wireOp",EDGE,"E7.0.3.3");Q33=makeQuery(id+"F3.imprint","IMPRINT",FACE,{"disambiguationData":[TD([[makeQuery(id+"F3.imprint","IMPRINT",EDGE,{"derivedFrom":subQ0}),-1.0]])]});}
            var Q34;
            {var subQ0=sQuery(id+"F3.wireOp",EDGE,"E7.2.4.3");Q34=makeQuery(id+"F3.imprint","IMPRINT",FACE,{"disambiguationData":[TD([[makeQuery(id+"F3.imprint","IMPRINT",EDGE,{"derivedFrom":subQ0}),-1.0]])]});}
            var Q35;
            {var subQ0=sQuery(id+"F3.wireOp",EDGE,"E7.2.5.3");Q35=makeQuery(id+"F3.imprint","IMPRINT",FACE,{"disambiguationData":[TD([[makeQuery(id+"F3.imprint","IMPRINT",EDGE,{"derivedFrom":subQ0}),-1.0]])]});}
            var Q36;
            {var subQ0=sQuery(id+"F3.wireOp",EDGE,"E7.2.6.3");Q36=makeQuery(id+"F3.imprint","IMPRINT",FACE,{"disambiguationData":[TD([[makeQuery(id+"F3.imprint","IMPRINT",EDGE,{"derivedFrom":subQ0}),-1.0]])]});}
            var Q37;
            {var subQ0=sQuery(id+"F3.wireOp",EDGE,"E7.1.4.3");Q37=makeQuery(id+"F3.imprint","IMPRINT",FACE,{"disambiguationData":[TD([[makeQuery(id+"F3.imprint","IMPRINT",EDGE,{"derivedFrom":subQ0}),-1.0]])]});}
            var Q38;
            {var subQ0=sQuery(id+"F3.wireOp",EDGE,"E7.1.5.3");Q38=makeQuery(id+"F3.imprint","IMPRINT",FACE,{"disambiguationData":[TD([[makeQuery(id+"F3.imprint","IMPRINT",EDGE,{"derivedFrom":subQ0}),-1.0]])]});}
            var Q39;
            {var subQ0=sQuery(id+"F3.wireOp",EDGE,"E7.1.6.3");Q39=makeQuery(id+"F3.imprint","IMPRINT",FACE,{"disambiguationData":[TD([[makeQuery(id+"F3.imprint","IMPRINT",EDGE,{"derivedFrom":subQ0}),-1.0]])]});}
            var Q40;
            {var subQ0=sQuery(id+"F3.wireOp",EDGE,"E7.0.4.3");Q40=makeQuery(id+"F3.imprint","IMPRINT",FACE,{"disambiguationData":[TD([[makeQuery(id+"F3.imprint","IMPRINT",EDGE,{"derivedFrom":subQ0}),-1.0]])]});}
            var Q41;
            {var subQ0=sQuery(id+"F3.wireOp",EDGE,"E7.0.5.3");Q41=makeQuery(id+"F3.imprint","IMPRINT",FACE,{"disambiguationData":[TD([[makeQuery(id+"F3.imprint","IMPRINT",EDGE,{"derivedFrom":subQ0}),-1.0]])]});}
            var Q42;
            {var subQ0=sQuery(id+"F3.wireOp",EDGE,"E7.0.6.3");Q42=makeQuery(id+"F3.imprint","IMPRINT",FACE,{"disambiguationData":[TD([[makeQuery(id+"F3.imprint","IMPRINT",EDGE,{"derivedFrom":subQ0}),-1.0]])]});}
            var Q43;
            {var subQ0=sQuery(id+"F3.wireOp",EDGE,"E7.0.7.3");Q43=makeQuery(id+"F3.imprint","IMPRINT",FACE,{"disambiguationData":[TD([[makeQuery(id+"F3.imprint","IMPRINT",EDGE,{"derivedFrom":subQ0}),-1.0]])]});}
            var Q44;
            {var subQ0=sQuery(id+"F3.wireOp",EDGE,"E7.0.8.3");Q44=makeQuery(id+"F3.imprint","IMPRINT",FACE,{"disambiguationData":[TD([[makeQuery(id+"F3.imprint","IMPRINT",EDGE,{"derivedFrom":subQ0}),-1.0]])]});}
            var Q45;
            {var subQ0=sQuery(id+"F3.wireOp",EDGE,"E7.0.9.3");Q45=makeQuery(id+"F3.imprint","IMPRINT",FACE,{"disambiguationData":[TD([[makeQuery(id+"F3.imprint","IMPRINT",EDGE,{"derivedFrom":subQ0}),-1.0]])]});}
            var Q46;
            {var subQ0=sQuery(id+"F3.wireOp",EDGE,"E7.0.10.3");Q46=makeQuery(id+"F3.imprint","IMPRINT",FACE,{"disambiguationData":[TD([[makeQuery(id+"F3.imprint","IMPRINT",EDGE,{"derivedFrom":subQ0}),-1.0]])]});}
            var Q47;
            {var subQ0=sQuery(id+"F3.wireOp",EDGE,"E7.1.7.3");Q47=makeQuery(id+"F3.imprint","IMPRINT",FACE,{"disambiguationData":[TD([[makeQuery(id+"F3.imprint","IMPRINT",EDGE,{"derivedFrom":subQ0}),-1.0]])]});}
            var Q48;
            {var subQ0=sQuery(id+"F3.wireOp",EDGE,"E7.1.8.3");Q48=makeQuery(id+"F3.imprint","IMPRINT",FACE,{"disambiguationData":[TD([[makeQuery(id+"F3.imprint","IMPRINT",EDGE,{"derivedFrom":subQ0}),-1.0]])]});}
            var Q49;
            {var subQ0=sQuery(id+"F3.wireOp",EDGE,"E7.1.9.3");Q49=makeQuery(id+"F3.imprint","IMPRINT",FACE,{"disambiguationData":[TD([[makeQuery(id+"F3.imprint","IMPRINT",EDGE,{"derivedFrom":subQ0}),-1.0]])]});}
            var Q50;
            {var subQ0=sQuery(id+"F3.wireOp",EDGE,"E7.1.10.3");Q50=makeQuery(id+"F3.imprint","IMPRINT",FACE,{"disambiguationData":[TD([[makeQuery(id+"F3.imprint","IMPRINT",EDGE,{"derivedFrom":subQ0}),-1.0]])]});}
            var Q51;
            {var subQ0=sQuery(id+"F3.wireOp",EDGE,"E7.2.10.3");Q51=makeQuery(id+"F3.imprint","IMPRINT",FACE,{"disambiguationData":[TD([[makeQuery(id+"F3.imprint","IMPRINT",EDGE,{"derivedFrom":subQ0}),-1.0]])]});}
            var Q52;
            {var subQ0=sQuery(id+"F3.wireOp",EDGE,"E7.2.9.3");Q52=makeQuery(id+"F3.imprint","IMPRINT",FACE,{"disambiguationData":[TD([[makeQuery(id+"F3.imprint","IMPRINT",EDGE,{"derivedFrom":subQ0}),-1.0]])]});}
            var Q53;
            {var subQ0=sQuery(id+"F3.wireOp",EDGE,"E7.2.8.3");Q53=makeQuery(id+"F3.imprint","IMPRINT",FACE,{"disambiguationData":[TD([[makeQuery(id+"F3.imprint","IMPRINT",EDGE,{"derivedFrom":subQ0}),-1.0]])]});}
            var Q54;
            {var subQ0=sQuery(id+"F3.wireOp",EDGE,"E7.2.7.3");Q54=makeQuery(id+"F3.imprint","IMPRINT",FACE,{"disambiguationData":[TD([[makeQuery(id+"F3.imprint","IMPRINT",EDGE,{"derivedFrom":subQ0}),-1.0]])]});}
            var Q55;
            {var subQ0=sQuery(id+"F3.wireOp",EDGE,"E7.0.11.3");Q55=makeQuery(id+"F3.imprint","IMPRINT",FACE,{"disambiguationData":[TD([[makeQuery(id+"F3.imprint","IMPRINT",EDGE,{"derivedFrom":subQ0}),-1.0]])]});}
            var Q56;
            {var subQ0=sQuery(id+"F3.wireOp",EDGE,"E7.0.12.3");Q56=makeQuery(id+"F3.imprint","IMPRINT",FACE,{"disambiguationData":[TD([[makeQuery(id+"F3.imprint","IMPRINT",EDGE,{"derivedFrom":subQ0}),-1.0]])]});}
            var Q57;
            {var subQ0=sQuery(id+"F3.wireOp",EDGE,"E7.0.13.3");Q57=makeQuery(id+"F3.imprint","IMPRINT",FACE,{"disambiguationData":[TD([[makeQuery(id+"F3.imprint","IMPRINT",EDGE,{"derivedFrom":subQ0}),-1.0]])]});}
            var Q58;
            {var subQ0=sQuery(id+"F3.wireOp",EDGE,"E7.0.14.3");Q58=makeQuery(id+"F3.imprint","IMPRINT",FACE,{"disambiguationData":[TD([[makeQuery(id+"F3.imprint","IMPRINT",EDGE,{"derivedFrom":subQ0}),-1.0]])]});}
            var Q59;
            {var subQ0=sQuery(id+"F3.wireOp",EDGE,"E7.0.15.3");Q59=makeQuery(id+"F3.imprint","IMPRINT",FACE,{"disambiguationData":[TD([[makeQuery(id+"F3.imprint","IMPRINT",EDGE,{"derivedFrom":subQ0}),-1.0]])]});}
            var Q60;
            {var subQ0=sQuery(id+"F3.wireOp",EDGE,"E7.0.16.3");Q60=makeQuery(id+"F3.imprint","IMPRINT",FACE,{"disambiguationData":[TD([[makeQuery(id+"F3.imprint","IMPRINT",EDGE,{"derivedFrom":subQ0}),-1.0]])]});}
            var Q61;
            {var subQ0=sQuery(id+"F3.wireOp",EDGE,"E7.0.17.3");Q61=makeQuery(id+"F3.imprint","IMPRINT",FACE,{"disambiguationData":[TD([[makeQuery(id+"F3.imprint","IMPRINT",EDGE,{"derivedFrom":subQ0}),-1.0]])]});}
            var Q62;
            {var subQ0=sQuery(id+"F3.wireOp",EDGE,"E7.0.18.3");Q62=makeQuery(id+"F3.imprint","IMPRINT",FACE,{"disambiguationData":[TD([[makeQuery(id+"F3.imprint","IMPRINT",EDGE,{"derivedFrom":subQ0}),-1.0]])]});}
            var Q63;
            {var subQ0=sQuery(id+"F3.wireOp",EDGE,"E7.0.19.3");Q63=makeQuery(id+"F3.imprint","IMPRINT",FACE,{"disambiguationData":[TD([[makeQuery(id+"F3.imprint","IMPRINT",EDGE,{"derivedFrom":subQ0}),-1.0]])]});}
            var Q64;
            {var subQ0=sQuery(id+"F3.wireOp",EDGE,"E7.0.20.3");Q64=makeQuery(id+"F3.imprint","IMPRINT",FACE,{"disambiguationData":[TD([[makeQuery(id+"F3.imprint","IMPRINT",EDGE,{"derivedFrom":subQ0}),-1.0]])]});}
            var Q65;
            {var subQ0=sQuery(id+"F3.wireOp",EDGE,"E7.0.21.3");Q65=makeQuery(id+"F3.imprint","IMPRINT",FACE,{"disambiguationData":[TD([[makeQuery(id+"F3.imprint","IMPRINT",EDGE,{"derivedFrom":subQ0}),-1.0]])]});}
            var Q66;
            {var subQ0=sQuery(id+"F3.wireOp",EDGE,"E7.1.21.3");Q66=makeQuery(id+"F3.imprint","IMPRINT",FACE,{"disambiguationData":[TD([[makeQuery(id+"F3.imprint","IMPRINT",EDGE,{"derivedFrom":subQ0}),-1.0]])]});}
            var Q67;
            {var subQ0=sQuery(id+"F3.wireOp",EDGE,"E7.1.20.3");Q67=makeQuery(id+"F3.imprint","IMPRINT",FACE,{"disambiguationData":[TD([[makeQuery(id+"F3.imprint","IMPRINT",EDGE,{"derivedFrom":subQ0}),-1.0]])]});}
            var Q68;
            {var subQ0=sQuery(id+"F3.wireOp",EDGE,"E7.1.19.3");Q68=makeQuery(id+"F3.imprint","IMPRINT",FACE,{"disambiguationData":[TD([[makeQuery(id+"F3.imprint","IMPRINT",EDGE,{"derivedFrom":subQ0}),-1.0]])]});}
            var Q69;
            {var subQ0=sQuery(id+"F3.wireOp",EDGE,"E7.1.18.3");Q69=makeQuery(id+"F3.imprint","IMPRINT",FACE,{"disambiguationData":[TD([[makeQuery(id+"F3.imprint","IMPRINT",EDGE,{"derivedFrom":subQ0}),-1.0]])]});}
            var Q70;
            {var subQ0=sQuery(id+"F3.wireOp",EDGE,"E7.1.17.3");Q70=makeQuery(id+"F3.imprint","IMPRINT",FACE,{"disambiguationData":[TD([[makeQuery(id+"F3.imprint","IMPRINT",EDGE,{"derivedFrom":subQ0}),-1.0]])]});}
            var Q71;
            {var subQ0=sQuery(id+"F3.wireOp",EDGE,"E7.1.16.3");Q71=makeQuery(id+"F3.imprint","IMPRINT",FACE,{"disambiguationData":[TD([[makeQuery(id+"F3.imprint","IMPRINT",EDGE,{"derivedFrom":subQ0}),-1.0]])]});}
            var Q72;
            {var subQ0=sQuery(id+"F3.wireOp",EDGE,"E7.1.15.3");Q72=makeQuery(id+"F3.imprint","IMPRINT",FACE,{"disambiguationData":[TD([[makeQuery(id+"F3.imprint","IMPRINT",EDGE,{"derivedFrom":subQ0}),-1.0]])]});}
            var Q73;
            {var subQ0=sQuery(id+"F3.wireOp",EDGE,"E7.1.14.3");Q73=makeQuery(id+"F3.imprint","IMPRINT",FACE,{"disambiguationData":[TD([[makeQuery(id+"F3.imprint","IMPRINT",EDGE,{"derivedFrom":subQ0}),-1.0]])]});}
            var Q74;
            {var subQ0=sQuery(id+"F3.wireOp",EDGE,"E7.1.13.3");Q74=makeQuery(id+"F3.imprint","IMPRINT",FACE,{"disambiguationData":[TD([[makeQuery(id+"F3.imprint","IMPRINT",EDGE,{"derivedFrom":subQ0}),-1.0]])]});}
            var Q75;
            {var subQ0=sQuery(id+"F3.wireOp",EDGE,"E7.1.12.3");Q75=makeQuery(id+"F3.imprint","IMPRINT",FACE,{"disambiguationData":[TD([[makeQuery(id+"F3.imprint","IMPRINT",EDGE,{"derivedFrom":subQ0}),-1.0]])]});}
            var Q76;
            {var subQ0=sQuery(id+"F3.wireOp",EDGE,"E7.1.11.3");Q76=makeQuery(id+"F3.imprint","IMPRINT",FACE,{"disambiguationData":[TD([[makeQuery(id+"F3.imprint","IMPRINT",EDGE,{"derivedFrom":subQ0}),-1.0]])]});}
            var Q77;
            {var subQ0=sQuery(id+"F3.wireOp",EDGE,"E7.2.11.3");Q77=makeQuery(id+"F3.imprint","IMPRINT",FACE,{"disambiguationData":[TD([[makeQuery(id+"F3.imprint","IMPRINT",EDGE,{"derivedFrom":subQ0}),-1.0]])]});}
            var Q78;
            {var subQ0=sQuery(id+"F3.wireOp",EDGE,"E7.2.12.3");Q78=makeQuery(id+"F3.imprint","IMPRINT",FACE,{"disambiguationData":[TD([[makeQuery(id+"F3.imprint","IMPRINT",EDGE,{"derivedFrom":subQ0}),-1.0]])]});}
            var Q79;
            {var subQ0=sQuery(id+"F3.wireOp",EDGE,"E7.2.13.3");Q79=makeQuery(id+"F3.imprint","IMPRINT",FACE,{"disambiguationData":[TD([[makeQuery(id+"F3.imprint","IMPRINT",EDGE,{"derivedFrom":subQ0}),-1.0]])]});}
            var Q80;
            {var subQ0=sQuery(id+"F3.wireOp",EDGE,"E7.2.14.3");Q80=makeQuery(id+"F3.imprint","IMPRINT",FACE,{"disambiguationData":[TD([[makeQuery(id+"F3.imprint","IMPRINT",EDGE,{"derivedFrom":subQ0}),-1.0]])]});}
            var Q81;
            {var subQ0=sQuery(id+"F3.wireOp",EDGE,"E7.2.15.3");Q81=makeQuery(id+"F3.imprint","IMPRINT",FACE,{"disambiguationData":[TD([[makeQuery(id+"F3.imprint","IMPRINT",EDGE,{"derivedFrom":subQ0}),-1.0]])]});}
            var Q82;
            {var subQ0=sQuery(id+"F3.wireOp",EDGE,"E7.2.16.3");Q82=makeQuery(id+"F3.imprint","IMPRINT",FACE,{"disambiguationData":[TD([[makeQuery(id+"F3.imprint","IMPRINT",EDGE,{"derivedFrom":subQ0}),-1.0]])]});}
            var Q83;
            {var subQ0=sQuery(id+"F3.wireOp",EDGE,"E7.2.17.3");Q83=makeQuery(id+"F3.imprint","IMPRINT",FACE,{"disambiguationData":[TD([[makeQuery(id+"F3.imprint","IMPRINT",EDGE,{"derivedFrom":subQ0}),-1.0]])]});}
            var Q84;
            {var subQ0=sQuery(id+"F3.wireOp",EDGE,"E7.2.18.3");Q84=makeQuery(id+"F3.imprint","IMPRINT",FACE,{"disambiguationData":[TD([[makeQuery(id+"F3.imprint","IMPRINT",EDGE,{"derivedFrom":subQ0}),-1.0]])]});}
            var Q85;
            {var subQ0=sQuery(id+"F3.wireOp",EDGE,"E7.2.19.3");Q85=makeQuery(id+"F3.imprint","IMPRINT",FACE,{"disambiguationData":[TD([[makeQuery(id+"F3.imprint","IMPRINT",EDGE,{"derivedFrom":subQ0}),-1.0]])]});}
            var Q86;
            {var subQ0=sQuery(id+"F3.wireOp",EDGE,"E7.2.20.3");Q86=makeQuery(id+"F3.imprint","IMPRINT",FACE,{"disambiguationData":[TD([[makeQuery(id+"F3.imprint","IMPRINT",EDGE,{"derivedFrom":subQ0}),-1.0]])]});}
            var Q87;
            {var subQ0=sQuery(id+"F3.wireOp",EDGE,"E7.2.21.3");Q87=makeQuery(id+"F3.imprint","IMPRINT",FACE,{"disambiguationData":[TD([[makeQuery(id+"F3.imprint","IMPRINT",EDGE,{"derivedFrom":subQ0}),-1.0]])]});}
            extrude(context, id + "F4", {"entities" : qUnion([Q0, Q1, Q2, Q3, Q4, Q5, Q6, Q7, Q8, Q9, Q10, Q11, Q12, Q13, Q14, Q15, Q16, Q17, Q18, Q19, Q20, Q21, Q22, Q23, Q24, Q25, Q26, Q27, Q28, Q29, Q30, Q31, Q32, Q33, Q34, Q35, Q36, Q37, Q38, Q39, Q40, Q41, Q42, Q43, Q44, Q45, Q46, Q47, Q48, Q49, Q50, Q51, Q52, Q53, Q54, Q55, Q56, Q57, Q58, Q59, Q60, Q61, Q62, Q63, Q64, Q65, Q66, Q67, Q68, Q69, Q70, Q71, Q72, Q73, Q74, Q75, Q76, Q77, Q78, Q79, Q80, Q81, Q82, Q83, Q84, Q85, Q86, Q87]), "operationType" : NewBodyOperationType.REMOVE, "oppositeDirection" : true, "depth" : 25.4 * mm, "offsetDistance" : 25.4 * mm});
        }
        {
            var Q0;
            {var subQ0=sQuery(id+"F0.wireOp",EDGE,"E0.left");Q0=makeQuery(id+"F2.opExtrude","CAP_EDGE",EDGE,{"disambiguationData":[OSD([subQ0]),TDD([makeQuery(id+"F0.imprint","IMPRINT",EDGE,{"disambiguationData":[TD([[makeQuery(id+"F0.imprint","INTERSECT",VERTEX,{"derivedFrom":[sQuery(id+"F0.wireOp",EDGE,"E0.bottom"),subQ0]}),-1.0]])],"derivedFrom":subQ0})])],"isStart":false});}
            var Q1;
            Q1=makeQuery(id+"F2.opExtrude","CAP_EDGE",EDGE,{"disambiguationData":[OSD([sQuery(id+"F0.wireOp",EDGE,"E0.bottom")])],"isStart":false});
            var Q2;
            {var subQ0=sQuery(id+"F0.wireOp",EDGE,"E0.right");Q2=makeQuery(id+"F2.opExtrude","CAP_EDGE",EDGE,{"disambiguationData":[OSD([subQ0]),TDD([makeQuery(id+"F0.imprint","IMPRINT",EDGE,{"disambiguationData":[TD([[makeQuery(id+"F0.imprint","INTERSECT",VERTEX,{"derivedFrom":[sQuery(id+"F0.wireOp",EDGE,"E0.bottom"),subQ0]}),-1.0]])],"derivedFrom":subQ0})])],"isStart":false});}
            var Q3;
            Q3=makeQuery(id+"F2.opExtrude","CAP_EDGE",EDGE,{"disambiguationData":[OSD([sQuery(id+"F0.wireOp",EDGE,"E5.top")])],"isStart":false});
            var Q4;
            Q4=makeQuery(id+"F2.opExtrude","CAP_EDGE",EDGE,{"disambiguationData":[OSD([sQuery(id+"F0.wireOp",EDGE,"E5.left")])],"isStart":false});
            var Q5;
            Q5=makeQuery(id+"F2.opExtrude","CAP_EDGE",EDGE,{"disambiguationData":[OSD([sQuery(id+"F0.wireOp",EDGE,"E4.top")])],"isStart":false});
            var Q6;
            Q6=makeQuery(id+"F2.opExtrude","CAP_EDGE",EDGE,{"disambiguationData":[OSD([sQuery(id+"F0.wireOp",EDGE,"E4.left")])],"isStart":false});
            var Q7;
            Q7=makeQuery(id+"F2.opExtrude","CAP_EDGE",EDGE,{"disambiguationData":[OSD([sQuery(id+"F0.wireOp",EDGE,"E4.bottom")])],"isStart":false});
            var Q8;
            {var subQ0=sQuery(id+"F0.wireOp",EDGE,"E0.left");Q8=makeQuery(id+"F2.opExtrude","CAP_EDGE",EDGE,{"disambiguationData":[OSD([subQ0]),TDD([makeQuery(id+"F0.imprint","IMPRINT",EDGE,{"disambiguationData":[TD([[makeQuery(id+"F0.imprint","INTERSECT",VERTEX,{"derivedFrom":[sQuery(id+"F0.wireOp",EDGE,"E0.top"),subQ0]}),1.0]])],"derivedFrom":subQ0})])],"isStart":false});}
            var Q9;
            Q9=makeQuery(id+"F2.opExtrude","CAP_EDGE",EDGE,{"disambiguationData":[OSD([sQuery(id+"F0.wireOp",EDGE,"E0.top")])],"isStart":false});
            var Q10;
            {var subQ0=sQuery(id+"F0.wireOp",EDGE,"E0.right");Q10=makeQuery(id+"F2.opExtrude","CAP_EDGE",EDGE,{"disambiguationData":[OSD([subQ0]),TDD([makeQuery(id+"F0.imprint","IMPRINT",EDGE,{"disambiguationData":[TD([[makeQuery(id+"F0.imprint","INTERSECT",VERTEX,{"derivedFrom":[sQuery(id+"F0.wireOp",EDGE,"E0.top"),subQ0]}),1.0]])],"derivedFrom":subQ0})])],"isStart":false});}
            var Q11;
            Q11=makeQuery(id+"F2.opExtrude","CAP_EDGE",EDGE,{"disambiguationData":[OSD([sQuery(id+"F0.wireOp",EDGE,"E5.bottom")])],"isStart":false});
            var Q12;
            Q12=makeQuery(id+"F2.opExtrude","SWEPT_EDGE",EDGE,{"disambiguationData":[OSD([sQuery(id+"F0.wireOp",EDGE,"E0.bottom"),sQuery(id+"F0.wireOp",EDGE,"E0.right")])]});
            var Q13;
            Q13=makeQuery(id+"F2.opExtrude","SWEPT_EDGE",EDGE,{"disambiguationData":[OSD([sQuery(id+"F0.wireOp",EDGE,"E0.bottom"),sQuery(id+"F0.wireOp",EDGE,"E0.left")])]});
            var Q14;
            Q14=makeQuery(id+"F2.opExtrude","SWEPT_EDGE",EDGE,{"disambiguationData":[OSD([sQuery(id+"F0.wireOp",EDGE,"E0.top"),sQuery(id+"F0.wireOp",EDGE,"E0.left")])]});
            var Q15;
            Q15=makeQuery(id+"F2.opExtrude","SWEPT_EDGE",EDGE,{"disambiguationData":[OSD([sQuery(id+"F0.wireOp",EDGE,"E0.top"),sQuery(id+"F0.wireOp",EDGE,"E0.right")])]});
            fillet(context, id + "F5", {"entities" : qUnion([Q0, Q1, Q2, Q3, Q4, Q5, Q6, Q7, Q8, Q9, Q10, Q11, Q12, Q13, Q14, Q15]), "radius" : 3.17 * mm, "tangentPropagation" : true, "allowEdgeOverflow" : false});
        }
        {
            var Q0;
            {var subQ0=sQuery(id+"F0.wireOp",EDGE,"E5.right");var subQ1=sQuery(id+"F0.wireOp",EDGE,"E4.right");var subQ2=sQuery(id+"F0.wireOp",EDGE,"E1.right");var subQ3=sQuery(id+"F0.wireOp",EDGE,"E1.left");var subQ4=sQuery(id+"F0.wireOp",EDGE,"E1.top");var subQ5=sQuery(id+"F0.wireOp",EDGE,"E1.bottom");Q0=makeQuery(id+"F2.boolean.opBoolean","MERGE",FACE,{"derivedFrom":[makeQuery(id+"F1.opExtrude","CAP_FACE",FACE,{"disambiguationData":[OSD([subQ5,subQ4,subQ3,subQ2,subQ1,subQ0])],"isStart":true}),makeQuery(id+"F2.opExtrude","CAP_FACE",FACE,{"disambiguationData":[OSD([sQuery(id+"F0.wireOp",EDGE,"E0.bottom"),sQuery(id+"F0.wireOp",EDGE,"E0.top"),sQuery(id+"F0.wireOp",EDGE,"E0.left"),sQuery(id+"F0.wireOp",EDGE,"E0.right"),subQ5,subQ4,subQ3,subQ2,sQuery(id+"F0.wireOp",EDGE,"E4.bottom"),sQuery(id+"F0.wireOp",EDGE,"E4.top"),sQuery(id+"F0.wireOp",EDGE,"E4.left"),subQ1,sQuery(id+"F0.wireOp",EDGE,"E5.bottom"),sQuery(id+"F0.wireOp",EDGE,"E5.top"),sQuery(id+"F0.wireOp",EDGE,"E5.left"),subQ0])],"isStart":true})]});}
            var sketch = newSketch(context, id + "F6", { "sketchPlane" : qUnion([Q0])});
            skLineSegment(sketch, "E8.bottom", {"start": v(-69.85, -25.14) * mm, "end": v(-63.5, -25.14) * mm});
            skLineSegment(sketch, "E8.top", {"start": v(-69.85, 25.66) * mm, "end": v(-63.5, 25.66) * mm});
            skLineSegment(sketch, "E8.left", {"start": v(-69.85, -25.14) * mm, "end": v(-69.85, 25.66) * mm});
            skLineSegment(sketch, "E8.right", {"start": v(-63.5, -25.14) * mm, "end": v(-63.5, 25.66) * mm});
            skLineSegment(sketch, "E9.bottom", {"start": v(69.85, -25.14) * mm, "end": v(63.5, -25.14) * mm});
            skLineSegment(sketch, "E9.top", {"start": v(69.85, 25.66) * mm, "end": v(63.5, 25.66) * mm});
            skLineSegment(sketch, "E9.left", {"start": v(69.85, -25.14) * mm, "end": v(69.85, 25.66) * mm});
            skLineSegment(sketch, "E9.right", {"start": v(63.5, -25.14) * mm, "end": v(63.5, 25.66) * mm});
            skSolve(sketch);
        }
        {
            var Q0;
            Q0=makeQuery(id+"F6.imprint","IMPRINT",FACE,{"disambiguationData":[TD([[makeQuery(id+"F6.imprint","IMPRINT",EDGE,{"derivedFrom":sQuery(id+"F6.wireOp",EDGE,"E8.bottom")}),1.0]])]});
            var Q1;
            Q1=makeQuery(id+"F6.imprint","IMPRINT",FACE,{"disambiguationData":[TD([[makeQuery(id+"F6.imprint","IMPRINT",EDGE,{"derivedFrom":sQuery(id+"F6.wireOp",EDGE,"E9.bottom")}),-1.0]])]});
            extrude(context, id + "F7", {"entities" : qUnion([Q0, Q1]), "operationType" : NewBodyOperationType.REMOVE, "oppositeDirection" : true, "depth" : 9.52 * mm, "offsetDistance" : 25.4 * mm});
        }
        {
            var Q0;
            Q0=makeQuery(id+"F2.opExtrude","SWEPT_FACE",FACE,{"disambiguationData":[OSD([sQuery(id+"F0.wireOp",EDGE,"E0.bottom")])]});
            var sketch = newSketch(context, id + "F8", { "sketchPlane" : qUnion([Q0])});
            skText(sketch, "E10", { "text": "1/8 x 1", "fontName": "OpenSans-Regular.ttf"});
            const initialGuessF8  = {"E10": [-0.05575, 0.00216, 1, 0, 0.01027]};
            skSetInitialGuess(sketch, initialGuessF8);
            skSolve(sketch);
        }
        {
            var Q0;
            Q0 = qSketchRegion(id + "F8", true);
            extrude(context, id + "F9", {"entities" : qUnion([Q0]), "operationType" : NewBodyOperationType.REMOVE, "oppositeDirection" : true, "depth" : 3.17 * mm, "offsetDistance" : 25.4 * mm});
        }
    });
